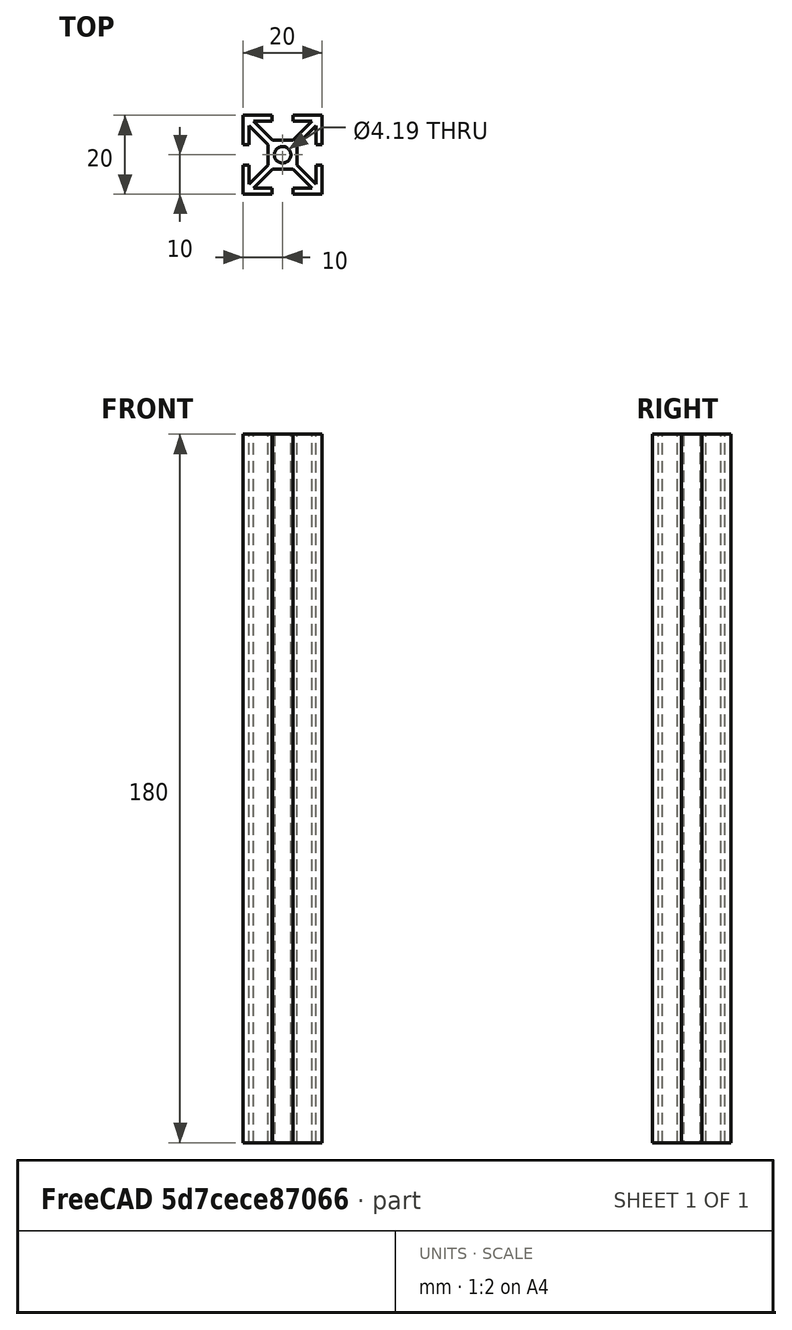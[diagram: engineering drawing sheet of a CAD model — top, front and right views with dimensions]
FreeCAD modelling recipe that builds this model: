
FCSTD DOCUMENT  (FreeCAD 0.15R4671 (Git))
Label: 20series-1x1_180mm
License: All rights reserved
LicenseURL: http://en.wikipedia.org/wiki/All_rights_reserved
objects: Sketcher::SketchObject×1, Part::Extrusion×1
note: 2 computed .brp shape members not serialized (recipe doc carries the construction recipe); baked Part::Feature solids carry a one-line shape summary decoded from their .brp

FEATURE [Sketcher::SketchObject] Sketch  label="20seriesProfile"
  sketch-geometry (93):
    g0: LineSegment [constr] StartX=0 StartY=0 StartZ=0 EndX=20 EndY=0 EndZ=0
    g1: LineSegment [constr] StartX=20 StartY=0 StartZ=0 EndX=20 EndY=20 EndZ=0
    g2: LineSegment [constr] StartX=20 StartY=20 StartZ=0 EndX=0 EndY=20 EndZ=0
    g3: LineSegment [constr] StartX=0 StartY=20 StartZ=0 EndX=0 EndY=0 EndZ=0
    g4: LineSegment [constr] StartX=0 StartY=0 StartZ=0 EndX=20 EndY=20 EndZ=0
    g5: LineSegment [constr] StartX=0 StartY=20 StartZ=0 EndX=20 EndY=0 EndZ=0
    g6: GeomPoint [constr] X=0 Y=10 Z=0
    g7: GeomPoint [constr] X=20 Y=10 Z=0
    g8: GeomPoint [constr] X=10 Y=20 Z=0
    g9: GeomPoint [constr] X=10 Y=0 Z=0
    g10: LineSegment [constr] StartX=0 StartY=10 StartZ=0 EndX=20 EndY=10 EndZ=0
    g11: LineSegment [constr] StartX=10 StartY=20 StartZ=0 EndX=10 EndY=0 EndZ=0
    g12: GeomPoint [constr] X=10 Y=10 Z=0
    g13: Circle CenterX=10 CenterY=10 CenterZ=0 NormalX=0 NormalY=0 NormalZ=1 Radius=2.095
    g14: LineSegment StartX=6.34 StartY=6.34 StartZ=0 EndX=13.66 EndY=6.34 EndZ=0
    g15: LineSegment StartX=13.66 StartY=6.34 StartZ=0 EndX=13.66 EndY=13.66 EndZ=0
    g16: LineSegment StartX=13.66 StartY=13.66 StartZ=0 EndX=6.34 EndY=13.66 EndZ=0
    g17: LineSegment StartX=6.34 StartY=13.66 StartZ=0 EndX=6.34 EndY=6.34 EndZ=0
    g18: LineSegment [constr] StartX=1.5 StartY=1.5 StartZ=0 EndX=18.5 EndY=1.5 EndZ=0
    g19: LineSegment [constr] StartX=18.5 StartY=1.5 StartZ=0 EndX=18.5 EndY=18.5 EndZ=0
    g20: LineSegment [constr] StartX=18.5 StartY=18.5 StartZ=0 EndX=1.5 EndY=18.5 EndZ=0
    g21: LineSegment [constr] StartX=1.5 StartY=18.5 StartZ=0 EndX=1.5 EndY=1.5 EndZ=0
    g22: LineSegment [constr] StartX=1.5 StartY=1.5 StartZ=0 EndX=0 EndY=1.5 EndZ=0
    g23: LineSegment [constr] StartX=2.56066 StartY=1.5 StartZ=0 EndX=7.40066 EndY=6.34 EndZ=0
    g24: LineSegment [constr] StartX=6.34 StartY=7.40066 StartZ=0 EndX=1.5 EndY=2.56066 EndZ=0
    g25: LineSegment [constr] StartX=1.5 StartY=2.56066 StartZ=0 EndX=2.56066 EndY=1.5 EndZ=0
    g26: LineSegment [constr] StartX=17.4393 StartY=1.5 StartZ=0 EndX=12.5993 EndY=6.34 EndZ=0
    g27: LineSegment [constr] StartX=13.66 StartY=7.40066 StartZ=0 EndX=18.5 EndY=2.56066 EndZ=0
    g28: LineSegment [constr] StartX=2.56066 StartY=18.5 StartZ=0 EndX=7.40066 EndY=13.66 EndZ=0
    g29: LineSegment [constr] StartX=1.5 StartY=17.4393 StartZ=0 EndX=6.34 EndY=12.5993 EndZ=0
    g30: LineSegment [constr] StartX=2.56066 StartY=18.5 StartZ=0 EndX=1.5 EndY=17.4393 EndZ=0
    g31: LineSegment [constr] StartX=18.5 StartY=2.56066 StartZ=0 EndX=17.4393 EndY=1.5 EndZ=0
    g32: LineSegment [constr] StartX=17.4393 StartY=18.5 StartZ=0 EndX=12.5993 EndY=13.66 EndZ=0
    g33: LineSegment [constr] StartX=13.66 StartY=12.5993 StartZ=0 EndX=18.5 EndY=17.4393 EndZ=0
    g34: LineSegment [constr] StartX=18.5 StartY=17.4393 StartZ=0 EndX=17.4393 EndY=18.5 EndZ=0
    g35: LineSegment [constr] StartX=0 StartY=7.37 StartZ=0 EndX=1.5 EndY=7.37 EndZ=0
    g36: LineSegment [constr] StartX=1.5 StartY=12.63 StartZ=0 EndX=0 EndY=12.63 EndZ=0
    g37: LineSegment [constr] StartX=0.75 StartY=12.63 StartZ=0 EndX=0.75 EndY=7.37 EndZ=0
    g38: GeomPoint [constr] X=0.75 Y=10 Z=0
    g39: LineSegment [constr] StartX=18.5 StartY=12.63 StartZ=0 EndX=20 EndY=12.63 EndZ=0
    g40: LineSegment [constr] StartX=18.5 StartY=7.37 StartZ=0 EndX=20 EndY=7.37 EndZ=0
    g41: LineSegment [constr] StartX=7.37 StartY=1.5 StartZ=0 EndX=7.37 EndY=0 EndZ=0
    g42: LineSegment [constr] StartX=12.63 StartY=1.5 StartZ=0 EndX=12.63 EndY=0 EndZ=0
    g43: LineSegment [constr] StartX=7.37 StartY=0.75 StartZ=0 EndX=12.63 EndY=0.75 EndZ=0
    g44: LineSegment [constr] StartX=7.37 StartY=20 StartZ=0 EndX=7.37 EndY=18.5 EndZ=0
    g45: LineSegment [constr] StartX=12.63 StartY=20 StartZ=0 EndX=12.63 EndY=18.5 EndZ=0
    g46: GeomPoint [constr] X=7.37 Y=19.25 Z=0
    g47: LineSegment [constr] StartX=7.37 StartY=19.25 StartZ=0 EndX=12.63 EndY=19.25 EndZ=0
    g48: GeomPoint [constr] X=19.25 Y=12.63 Z=0
    g49: LineSegment [constr] StartX=19.25 StartY=12.63 StartZ=0 EndX=19.25 EndY=7.37 EndZ=0
    g50: GeomPoint [constr] X=19.25 Y=10 Z=0
    g51: GeomPoint [constr] X=10 Y=19.25 Z=0
    g52: GeomPoint [constr] X=10 Y=0.75 Z=0
    g53: LineSegment StartX=0 StartY=7.37 StartZ=0 EndX=0 EndY=0 EndZ=0
    g54: LineSegment StartX=0 StartY=0 StartZ=0 EndX=7.37 EndY=0 EndZ=0
    g55: LineSegment StartX=7.37 StartY=0 StartZ=0 EndX=7.37 EndY=1.5 EndZ=0
    g56: LineSegment StartX=7.37 StartY=1.5 StartZ=0 EndX=2.56066 EndY=1.5 EndZ=0
    g57: LineSegment StartX=2.56066 StartY=1.5 StartZ=0 EndX=7.40066 EndY=6.34 EndZ=0
    g58: LineSegment StartX=7.40066 StartY=6.34 StartZ=0 EndX=6.34 EndY=6.34 EndZ=0
    g59: LineSegment StartX=6.34 StartY=6.34 StartZ=0 EndX=6.34 EndY=7.40066 EndZ=0
    g60: LineSegment StartX=6.34 StartY=7.40066 StartZ=0 EndX=1.5 EndY=2.56066 EndZ=0
    g61: LineSegment StartX=1.5 StartY=2.56066 StartZ=0 EndX=1.5 EndY=7.37 EndZ=0
    g62: LineSegment StartX=1.5 StartY=7.37 StartZ=0 EndX=0 EndY=7.37 EndZ=0
    g63: LineSegment StartX=20 StartY=7.37 StartZ=0 EndX=20 EndY=0 EndZ=0
    g64: LineSegment StartX=20 StartY=0 StartZ=0 EndX=12.63 EndY=0 EndZ=0
    g65: LineSegment StartX=12.63 StartY=0 StartZ=0 EndX=12.63 EndY=1.5 EndZ=0
    g66: LineSegment StartX=12.63 StartY=1.5 StartZ=0 EndX=17.4393 EndY=1.5 EndZ=0
    g67: LineSegment StartX=17.4393 StartY=1.5 StartZ=0 EndX=12.5993 EndY=6.34 EndZ=0
    g68: LineSegment StartX=12.5993 StartY=6.34 StartZ=0 EndX=13.66 EndY=6.34 EndZ=0
    g69: LineSegment StartX=13.66 StartY=6.34 StartZ=0 EndX=13.66 EndY=7.40066 EndZ=0
    g70: LineSegment StartX=13.66 StartY=7.40066 StartZ=0 EndX=18.5 EndY=2.56066 EndZ=0
    g71: LineSegment StartX=18.5 StartY=2.56066 StartZ=0 EndX=18.5 EndY=7.37 EndZ=0
    g72: LineSegment StartX=18.5 StartY=7.37 StartZ=0 EndX=20 EndY=7.37 EndZ=0
    g73: LineSegment StartX=1.5 StartY=12.63 StartZ=0 EndX=1.5 EndY=17.4393 EndZ=0
    g74: LineSegment StartX=1.5 StartY=17.4393 StartZ=0 EndX=6.34 EndY=12.5993 EndZ=0
    g75: LineSegment StartX=6.34 StartY=12.5993 StartZ=0 EndX=6.34 EndY=13.66 EndZ=0
    g76: LineSegment StartX=6.34 StartY=13.66 StartZ=0 EndX=7.40066 EndY=13.66 EndZ=0
    g77: LineSegment StartX=7.40066 StartY=13.66 StartZ=0 EndX=2.56066 EndY=18.5 EndZ=0
    g78: LineSegment StartX=2.56066 StartY=18.5 StartZ=0 EndX=7.37 EndY=18.5 EndZ=0
    g79: LineSegment StartX=7.37 StartY=18.5 StartZ=0 EndX=7.37 EndY=20 EndZ=0
    g80: LineSegment StartX=7.37 StartY=20 StartZ=0 EndX=0 EndY=20 EndZ=0
    g81: LineSegment StartX=0 StartY=20 StartZ=0 EndX=0 EndY=12.63 EndZ=0
    g82: LineSegment StartX=0 StartY=12.63 StartZ=0 EndX=1.5 EndY=12.63 EndZ=0
    g83: LineSegment StartX=20 StartY=12.63 StartZ=0 EndX=20 EndY=20 EndZ=0
    g84: LineSegment StartX=20 StartY=20 StartZ=0 EndX=12.63 EndY=20 EndZ=0
    g85: LineSegment StartX=12.63 StartY=20 StartZ=0 EndX=12.63 EndY=18.5 EndZ=0
    g86: LineSegment StartX=12.63 StartY=18.5 StartZ=0 EndX=17.4393 EndY=18.5 EndZ=0
    g87: LineSegment StartX=17.4393 StartY=18.5 StartZ=0 EndX=12.5993 EndY=13.66 EndZ=0
    g88: LineSegment StartX=12.5993 StartY=13.66 StartZ=0 EndX=13.66 EndY=13.66 EndZ=0
    g89: LineSegment StartX=13.66 StartY=13.66 StartZ=0 EndX=13.66 EndY=12.5993 EndZ=0
    g90: LineSegment StartX=13.66 StartY=12.5993 StartZ=0 EndX=18.5 EndY=17.4393 EndZ=0
    g91: LineSegment StartX=18.5 StartY=17.4393 StartZ=0 EndX=18.5 EndY=12.63 EndZ=0
    g92: LineSegment StartX=18.5 StartY=12.63 StartZ=0 EndX=20 EndY=12.63 EndZ=0
  constraints (233):
    c: Coincident(g0,g1)
    c: Coincident(g1,g2)
    c: Coincident(g2,g3)
    c: Coincident(g3,g0)
    c: Horizontal(g0)
    c: Vertical(g1)
    c: Coincident(g0,g-1)
    c: Equal(g0,g3)
    c: DistanceX(g0) = 20
    c: Coincident(g4,g-1)
    c: Coincident(g4,g1)
    c: Coincident(g5,g2)
    c: Coincident(g5,g0)
    c: PointOnObject(g8,g2)
    c: Symmetric(g0,g0,g9)
    c: Symmetric(g1,g1,g7)
    c: Symmetric(g2,g2,g8)
    c: Symmetric(g3,g3,g6)
    c: Horizontal(g10)
    c: Coincident(g10,g7)
    c: Coincident(g10,g6)
    c: PointOnObject(g11,g2)
    c: PointOnObject(g11,g0)
    c: Vertical(g11)
    c: Coincident(g11,g9)
    c: PointOnObject(g12,g11)
    c: Symmetric(g10,g10,g12)
    c: Radius(g13) = 2.095
    c: Coincident(g13,g12)
    c: Coincident(g14,g15)
    c: Coincident(g15,g16)
    c: Coincident(g16,g17)
    c: Coincident(g17,g14)
    c: Horizontal(g14)
    c: Horizontal(g16)
    c: Vertical(g15)
    c: Vertical(g17)
    c: PointOnObject(g14,g4)
    c: PointOnObject(g15,g4)
    c: PointOnObject(g14,g5)
    c: DistanceX(g14) = 7.32
    c: Coincident(g18,g19)
    c: Coincident(g19,g20)
    c: Coincident(g20,g21)
    c: Coincident(g21,g18)
    c: Horizontal(g18)
    c: Vertical(g21)
    c: PointOnObject(g18,g4)
    c: PointOnObject(g19,g4)
    c: Equal(g21,g18)
    c: PointOnObject(g20,g5)
    c: Coincident(g22,g18)
    c: PointOnObject(g22,g3)
    c: Horizontal(g22)
    c: DistanceX(g22) = -1.5
    c: PointOnObject(g23,g14)
    c: Parallel(g23,g4)
    c: PointOnObject(g24,g17)
    c: PointOnObject(g24,g21)
    c: Parallel(g24,g4)
    c: PointOnObject(g23,g18)
    c: Coincident(g25,g24)
    c: Coincident(g25,g23)
    c: Perpendicular(g4,g25)
    c: Distance(g25) = 1.5
    c: PointOnObject(g26,g18)
    c: PointOnObject(g26,g14)
    c: PointOnObject(g27,g15)
    c: PointOnObject(g27,g19)
    c: PointOnObject(g28,g20)
    c: PointOnObject(g28,g16)
    c: PointOnObject(g29,g21)
    c: PointOnObject(g29,g17)
    c: Parallel(g29,g28)
    c: Parallel(g28,g27)
    c: Parallel(g27,g26)
    c: Parallel(g26,g5)
    c: Coincident(g30,g28)
    c: Coincident(g29,g30)
    c: Coincident(g31,g27)
    c: Coincident(g31,g26)
    c: Perpendicular(g5,g31)
    c: Perpendicular(g5,g30)
    c: Equal(g31,g30)
    c: Equal(g30,g25)
    c: PointOnObject(g32,g20)
    c: PointOnObject(g32,g16)
    c: PointOnObject(g33,g15)
    c: PointOnObject(g33,g19)
    c: Coincident(g34,g33)
    c: Parallel(g33,g32)
    c: Parallel(g32,g4)
    c: Coincident(g34,g32)
    c: Perpendicular(g4,g34)
    c: Equal(g34,g25)
    c: PointOnObject(g35,g3)
    c: PointOnObject(g35,g21)
    c: Horizontal(g35)
    c: PointOnObject(g36,g21)
    c: Horizontal(g36)
    c: Vertical(g37)
    c: Symmetric(g37,g37,g38)
    c: PointOnObject(g38,g10)
    c: PointOnObject(g37,g36)
    c: PointOnObject(g37,g35)
    c: Symmetric(g36,g36,g37)
    c: PointOnObject(g36,g3)
    c: DistanceY(g36,g35) = -5.26
    c: PointOnObject(g39,g19)
    c: PointOnObject(g39,g1)
    c: Horizontal(g39)
    c: PointOnObject(g40,g19)
    c: PointOnObject(g40,g1)
    c: Horizontal(g40)
    c: PointOnObject(g41,g18)
    c: PointOnObject(g41,g0)
    c: Vertical(g41)
    c: PointOnObject(g42,g18)
    c: PointOnObject(g42,g0)
    c: Vertical(g42)
    c: PointOnObject(g43,g41)
    c: PointOnObject(g43,g42)
    c: Horizontal(g43)
    c: Symmetric(g41,g41,g43)
    c: PointOnObject(g44,g2)
    c: PointOnObject(g44,g20)
    c: Vertical(g44)
    c: Vertical(g45)
    c: PointOnObject(g46,g44)
    c: Coincident(g47,g46)
    c: PointOnObject(g47,g45)
    c: Horizontal(g47)
    c: Symmetric(g44,g44,g46)
    c: PointOnObject(g48,g39)
    c: Coincident(g49,g48)
    c: PointOnObject(g49,g40)
    c: Vertical(g49)
    c: Symmetric(g39,g39,g48)
    c: PointOnObject(g50,g49)
    c: PointOnObject(g50,g10)
    c: PointOnObject(g51,g47)
    c: Symmetric(g47,g47,g51)
    c: PointOnObject(g51,g11)
    c: Equal(g47,g49)
    c: Equal(g49,g43)
    c: PointOnObject(g52,g43)
    c: Symmetric(g43,g43,g52)
    c: PointOnObject(g52,g11)
    c: Equal(g37,g47)
    c: Symmetric(g49,g49,g50)
    c: PointOnObject(g45,g2)
    c: PointOnObject(g45,g20)
    c: Coincident(g35,g53)
    c: Coincident(g53,g-1)
    c: Coincident(g53,g54)
    c: Coincident(g54,g41)
    c: Coincident(g54,g55)
    c: Coincident(g55,g41)
    c: Coincident(g55,g56)
    c: Coincident(g56,g23)
    c: Coincident(g56,g57)
    c: Coincident(g57,g23)
    c: Coincident(g57,g58)
    c: Coincident(g58,g14)
    c: Coincident(g58,g59)
    c: Coincident(g59,g24)
    c: Coincident(g59,g60)
    c: Coincident(g60,g24)
    c: Coincident(g60,g61)
    c: Coincident(g61,g35)
    c: Coincident(g61,g62)
    c: Coincident(g62,g53)
    c: Coincident(g40,g63)
    c: Coincident(g63,g0)
    c: Coincident(g63,g64)
    c: Coincident(g64,g42)
    c: Coincident(g64,g65)
    c: Coincident(g65,g42)
    c: Coincident(g65,g66)
    c: Coincident(g66,g26)
    c: Coincident(g66,g67)
    c: Coincident(g67,g26)
    c: Coincident(g67,g68)
    c: Coincident(g68,g14)
    c: Coincident(g68,g69)
    c: Coincident(g69,g27)
    c: Coincident(g69,g70)
    c: Coincident(g70,g27)
    c: Coincident(g70,g71)
    c: Coincident(g71,g40)
    c: Coincident(g71,g72)
    c: Coincident(g72,g63)
    c: Coincident(g36,g73)
    c: Coincident(g73,g29)
    c: Coincident(g73,g74)
    c: Coincident(g74,g29)
    c: Coincident(g74,g75)
    c: Coincident(g75,g16)
    c: Coincident(g75,g76)
    c: Coincident(g76,g28)
    c: Coincident(g76,g77)
    c: Coincident(g77,g28)
    c: Coincident(g77,g78)
    c: Coincident(g78,g44)
    c: Coincident(g78,g79)
    c: Coincident(g79,g44)
    c: Coincident(g79,g80)
    c: Coincident(g80,g2)
    c: Coincident(g80,g81)
    c: Coincident(g81,g36)
    c: Coincident(g81,g82)
    c: Coincident(g82,g73)
    c: Coincident(g39,g83)
    c: Coincident(g83,g1)
    c: Coincident(g83,g84)
    c: Coincident(g84,g45)
    c: Coincident(g84,g85)
    c: Coincident(g85,g45)
    c: Coincident(g85,g86)
    c: Coincident(g86,g32)
    c: Horizontal(g86)
    c: Coincident(g86,g87)
    c: Coincident(g87,g32)
    c: Coincident(g87,g88)
    c: Coincident(g88,g15)
    c: Coincident(g88,g89)
    c: Coincident(g89,g90)
    c: Coincident(g90,g33)
    c: Coincident(g90,g91)
    c: Coincident(g91,g39)
    c: Coincident(g91,g92)
    c: Coincident(g92,g83)
    c: Coincident(g89,g33)
FEATURE [Part::Extrusion] Extrude
  Base = -> Sketch
  Dir = (0,0,180)
  Solid = true
